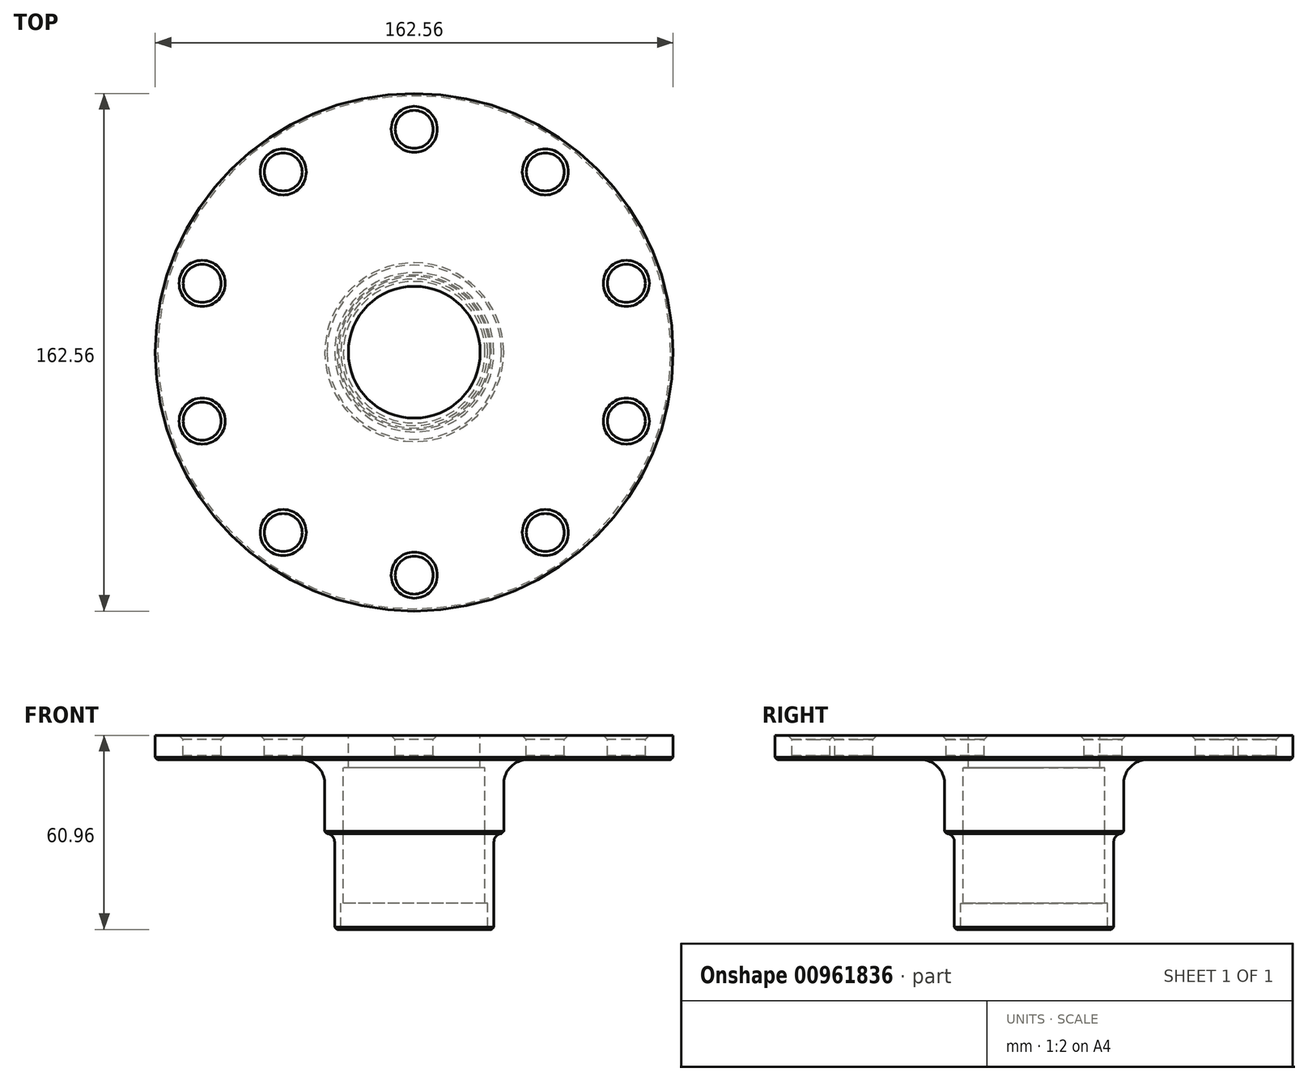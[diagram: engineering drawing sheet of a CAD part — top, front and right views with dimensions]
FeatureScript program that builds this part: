
annotation { "Feature Type Name" : "Feature", "Feature Type Description" : "" }
export const myFeature = defineFeature(function(context is Context, id is Id, definition is map)
    precondition{}
    {
        {
            var Q0;
            Q0=qCreatedBy(makeId("Top.planeOp"),FACE);
            var sketch = newSketch(context, id + "F0", { "sketchPlane" : qUnion([Q0])});
            skCircle(sketch, "E0", {"center": v(0, 0) * mm, "radius": 81.28 * mm});
            skCircle(sketch, "E1", {"center": v(0, 0) * mm, "radius": 28.08 * mm});
            skCircle(sketch, "E2", {"center": v(0, 0) * mm, "radius": 25.02 * mm});
            skCircle(sketch, "E3", {"center": v(0, 0) * mm, "radius": 69.99 * mm, "construction": true});
            skLineSegment(sketch, "E4", {"start": v(0, 0) * mm, "end": v(0, 86.5) * mm, "construction": true});
            skCircle(sketch, "E5", {"center": v(0, 69.99) * mm, "radius": 5.97 * mm});
            skCircle(sketch, "E6.1.0", {"center": v(-41.14, 56.62) * mm, "radius": 5.97 * mm});
            skCircle(sketch, "E6.2.0", {"center": v(-66.56, 21.63) * mm, "radius": 5.97 * mm});
            skCircle(sketch, "E6.3.0", {"center": v(-66.56, -21.63) * mm, "radius": 5.97 * mm});
            skCircle(sketch, "E6.4.0", {"center": v(-41.14, -56.62) * mm, "radius": 5.97 * mm});
            skCircle(sketch, "E6.5.0", {"center": v(0, -69.99) * mm, "radius": 5.97 * mm});
            skCircle(sketch, "E6.6.0", {"center": v(41.14, -56.62) * mm, "radius": 5.97 * mm});
            skCircle(sketch, "E6.7.0", {"center": v(66.56, -21.63) * mm, "radius": 5.97 * mm});
            skCircle(sketch, "E6.8.0", {"center": v(66.56, 21.63) * mm, "radius": 5.97 * mm});
            skCircle(sketch, "E6.9.0", {"center": v(41.14, 56.62) * mm, "radius": 5.97 * mm});
            skCircle(sketch, "E7", {"center": v(0, 0) * mm, "radius": 23 * mm});
            skCircle(sketch, "E8", {"center": v(0, 0) * mm, "radius": 22.23 * mm});
            skCircle(sketch, "E9", {"center": v(0, 0) * mm, "radius": 20.69 * mm});
            skSolve(sketch);
        }
        {
            var Q0;
            Q0=makeQuery(id+"F0.imprint","IMPRINT",FACE,{"disambiguationData":[TD([[makeQuery(id+"F0.imprint","IMPRINT",EDGE,{"derivedFrom":sQuery(id+"F0.wireOp",EDGE,"E0")}),1.0]])]});
            var Q1;
            Q1=makeQuery(id+"F0.imprint","IMPRINT",FACE,{"disambiguationData":[TD([[makeQuery(id+"F0.imprint","IMPRINT",EDGE,{"derivedFrom":sQuery(id+"F0.wireOp",EDGE,"E1")}),1.0]])]});
            var Q2;
            Q2=makeQuery(id+"F0.imprint","IMPRINT",FACE,{"disambiguationData":[TD([[makeQuery(id+"F0.imprint","IMPRINT",EDGE,{"derivedFrom":sQuery(id+"F0.wireOp",EDGE,"E2")}),1.0]])]});
            var Q3;
            Q3=makeQuery(id+"F0.imprint","IMPRINT",FACE,{"disambiguationData":[TD([[makeQuery(id+"F0.imprint","IMPRINT",EDGE,{"derivedFrom":sQuery(id+"F0.wireOp",EDGE,"E7")}),1.0]])]});
            var Q4;
            Q4=makeQuery(id+"F0.imprint","IMPRINT",FACE,{"disambiguationData":[TD([[makeQuery(id+"F0.imprint","IMPRINT",EDGE,{"derivedFrom":sQuery(id+"F0.wireOp",EDGE,"E8")}),1.0]])]});
            extrude(context, id + "F1", {"entities" : qUnion([Q0, Q1, Q2, Q3, Q4]), "oppositeDirection" : true, "depth" : 7.62 * mm, "offsetDistance" : 25.4 * mm});
        }
        {
            var Q0;
            Q0=makeQuery(id+"F1.opExtrude","CAP_EDGE",EDGE,{"disambiguationData":[OSD([sQuery(id+"F0.wireOp",EDGE,"E6.9.0")])],"isStart":true});
            var Q1;
            Q1=makeQuery(id+"F1.opExtrude","CAP_EDGE",EDGE,{"disambiguationData":[OSD([sQuery(id+"F0.wireOp",EDGE,"E5")])],"isStart":true});
            var Q2;
            Q2=makeQuery(id+"F1.opExtrude","CAP_EDGE",EDGE,{"disambiguationData":[OSD([sQuery(id+"F0.wireOp",EDGE,"E6.1.0")])],"isStart":true});
            var Q3;
            Q3=makeQuery(id+"F1.opExtrude","CAP_EDGE",EDGE,{"disambiguationData":[OSD([sQuery(id+"F0.wireOp",EDGE,"E6.2.0")])],"isStart":true});
            var Q4;
            Q4=makeQuery(id+"F1.opExtrude","CAP_EDGE",EDGE,{"disambiguationData":[OSD([sQuery(id+"F0.wireOp",EDGE,"E6.3.0")])],"isStart":true});
            var Q5;
            Q5=makeQuery(id+"F1.opExtrude","CAP_EDGE",EDGE,{"disambiguationData":[OSD([sQuery(id+"F0.wireOp",EDGE,"E6.4.0")])],"isStart":true});
            var Q6;
            Q6=makeQuery(id+"F1.opExtrude","CAP_EDGE",EDGE,{"disambiguationData":[OSD([sQuery(id+"F0.wireOp",EDGE,"E6.5.0")])],"isStart":true});
            var Q7;
            Q7=makeQuery(id+"F1.opExtrude","CAP_EDGE",EDGE,{"disambiguationData":[OSD([sQuery(id+"F0.wireOp",EDGE,"E6.6.0")])],"isStart":true});
            var Q8;
            Q8=makeQuery(id+"F1.opExtrude","CAP_EDGE",EDGE,{"disambiguationData":[OSD([sQuery(id+"F0.wireOp",EDGE,"E6.7.0")])],"isStart":true});
            var Q9;
            Q9=makeQuery(id+"F1.opExtrude","CAP_EDGE",EDGE,{"disambiguationData":[OSD([sQuery(id+"F0.wireOp",EDGE,"E6.8.0")])],"isStart":true});
            var Q10;
            Q10=makeQuery(id+"F1.opExtrude","CAP_EDGE",EDGE,{"disambiguationData":[OSD([sQuery(id+"F0.wireOp",EDGE,"E6.7.0")])],"isStart":false});
            var Q11;
            Q11=makeQuery(id+"F1.opExtrude","CAP_EDGE",EDGE,{"disambiguationData":[OSD([sQuery(id+"F0.wireOp",EDGE,"E6.8.0")])],"isStart":false});
            var Q12;
            Q12=makeQuery(id+"F1.opExtrude","CAP_EDGE",EDGE,{"disambiguationData":[OSD([sQuery(id+"F0.wireOp",EDGE,"E6.6.0")])],"isStart":false});
            var Q13;
            Q13=makeQuery(id+"F1.opExtrude","CAP_EDGE",EDGE,{"disambiguationData":[OSD([sQuery(id+"F0.wireOp",EDGE,"E6.5.0")])],"isStart":false});
            var Q14;
            Q14=makeQuery(id+"F1.opExtrude","CAP_EDGE",EDGE,{"disambiguationData":[OSD([sQuery(id+"F0.wireOp",EDGE,"E6.4.0")])],"isStart":false});
            var Q15;
            Q15=makeQuery(id+"F1.opExtrude","CAP_EDGE",EDGE,{"disambiguationData":[OSD([sQuery(id+"F0.wireOp",EDGE,"E6.3.0")])],"isStart":false});
            var Q16;
            Q16=makeQuery(id+"F1.opExtrude","CAP_EDGE",EDGE,{"disambiguationData":[OSD([sQuery(id+"F0.wireOp",EDGE,"E6.2.0")])],"isStart":false});
            var Q17;
            Q17=makeQuery(id+"F1.opExtrude","CAP_EDGE",EDGE,{"disambiguationData":[OSD([sQuery(id+"F0.wireOp",EDGE,"E6.1.0")])],"isStart":false});
            var Q18;
            Q18=makeQuery(id+"F1.opExtrude","CAP_EDGE",EDGE,{"disambiguationData":[OSD([sQuery(id+"F0.wireOp",EDGE,"E5")])],"isStart":false});
            var Q19;
            Q19=makeQuery(id+"F1.opExtrude","CAP_EDGE",EDGE,{"disambiguationData":[OSD([sQuery(id+"F0.wireOp",EDGE,"E6.9.0")])],"isStart":false});
            chamfer(context, id + "F2", {"entities" : qUnion([Q0, Q1, Q2, Q3, Q4, Q5, Q6, Q7, Q8, Q9, Q10, Q11, Q12, Q13, Q14, Q15, Q16, Q17, Q18, Q19]), "width" : 1.27 * mm, "tangentPropagation" : true});
        }
        {
            var Q0;
            Q0=makeQuery(id+"F0.imprint","IMPRINT",FACE,{"disambiguationData":[TD([[makeQuery(id+"F0.imprint","IMPRINT",EDGE,{"derivedFrom":sQuery(id+"F0.wireOp",EDGE,"E1")}),1.0]])]});
            var Q1;
            Q1=makeQuery(id+"F0.imprint","IMPRINT",FACE,{"disambiguationData":[TD([[makeQuery(id+"F0.imprint","IMPRINT",EDGE,{"derivedFrom":sQuery(id+"F0.wireOp",EDGE,"E2")}),1.0]])]});
            extrude(context, id + "F3", {"entities" : qUnion([Q0, Q1]), "operationType" : NewBodyOperationType.ADD, "oppositeDirection" : true, "depth" : 30.86 * mm, "offsetDistance" : 25.4 * mm});
        }
        {
            var Q0;
            Q0=makeQuery(id+"F0.imprint","IMPRINT",FACE,{"disambiguationData":[TD([[makeQuery(id+"F0.imprint","IMPRINT",EDGE,{"derivedFrom":sQuery(id+"F0.wireOp",EDGE,"E2")}),1.0]])]});
            extrude(context, id + "F4", {"entities" : qUnion([Q0]), "operationType" : NewBodyOperationType.ADD, "oppositeDirection" : true, "depth" : 60.96 * mm, "offsetDistance" : 25.4 * mm});
        }
        {
            var Q0;
            Q0=makeQuery(id+"F3.boolean.opBoolean","INTERSECT",EDGE,{"derivedFrom":[makeQuery(id+"F1.opExtrude","CAP_FACE",FACE,{"disambiguationData":[OSD([sQuery(id+"F0.wireOp",EDGE,"E0"),sQuery(id+"F0.wireOp",EDGE,"E5"),sQuery(id+"F0.wireOp",EDGE,"E6.1.0"),sQuery(id+"F0.wireOp",EDGE,"E6.2.0"),sQuery(id+"F0.wireOp",EDGE,"E6.3.0"),sQuery(id+"F0.wireOp",EDGE,"E6.4.0"),sQuery(id+"F0.wireOp",EDGE,"E6.5.0"),sQuery(id+"F0.wireOp",EDGE,"E6.6.0"),sQuery(id+"F0.wireOp",EDGE,"E6.7.0"),sQuery(id+"F0.wireOp",EDGE,"E6.8.0"),sQuery(id+"F0.wireOp",EDGE,"E6.9.0"),sQuery(id+"F0.wireOp",EDGE,"E9")])],"isStart":false}),makeQuery(id+"F3.opExtrude","SWEPT_FACE",FACE,{"disambiguationData":[OSD([sQuery(id+"F0.wireOp",EDGE,"E1")])]})]});
            fillet(context, id + "F5", {"entities" : qUnion([Q0]), "radius" : 7.62 * mm, "tangentPropagation" : true, "allowEdgeOverflow" : false});
        }
        {
            var Q0;
            Q0=makeQuery(id+"F4.boolean.opBoolean","INTERSECT",EDGE,{"derivedFrom":[makeQuery(id+"F3.opExtrude","CAP_FACE",FACE,{"disambiguationData":[OSD([sQuery(id+"F0.wireOp",EDGE,"E1"),sQuery(id+"F0.wireOp",EDGE,"E7")])],"isStart":false}),makeQuery(id+"F4.opExtrude","SWEPT_FACE",FACE,{"disambiguationData":[OSD([sQuery(id+"F0.wireOp",EDGE,"E2")])]})]});
            fillet(context, id + "F6", {"entities" : qUnion([Q0]), "radius" : 2.54 * mm, "tangentPropagation" : true, "allowEdgeOverflow" : false});
        }
        {
            var Q0;
            Q0=makeQuery(id+"F1.opExtrude","CAP_EDGE",EDGE,{"disambiguationData":[OSD([sQuery(id+"F0.wireOp",EDGE,"E0")])],"isStart":false});
            var Q1;
            Q1=makeQuery(id+"F3.opExtrude","CAP_EDGE",EDGE,{"disambiguationData":[OSD([sQuery(id+"F0.wireOp",EDGE,"E1")])],"isStart":false});
            var Q2;
            Q2=makeQuery(id+"F4.opExtrude","CAP_EDGE",EDGE,{"disambiguationData":[OSD([sQuery(id+"F0.wireOp",EDGE,"E2")])],"isStart":false});
            var Q3;
            Q3=makeQuery(id+"F4.opExtrude","CAP_EDGE",EDGE,{"disambiguationData":[OSD([sQuery(id+"F0.wireOp",EDGE,"E7")])],"isStart":false});
            chamfer(context, id + "F7", {"entities" : qUnion([Q0, Q1, Q2, Q3]), "width" : 0.76 * mm, "tangentPropagation" : true});
        }
        {
            var Q0;
            Q0=makeQuery(id+"F0.imprint","IMPRINT",FACE,{"disambiguationData":[TD([[makeQuery(id+"F0.imprint","IMPRINT",EDGE,{"derivedFrom":sQuery(id+"F0.wireOp",EDGE,"E8")}),1.0]])]});
            extrude(context, id + "F8", {"entities" : qUnion([Q0]), "operationType" : NewBodyOperationType.ADD, "oppositeDirection" : true, "depth" : 10.16 * mm, "offsetDistance" : 25.4 * mm});
        }
        {
            var Q0;
            {var subQ0=sQuery(id+"F0.wireOp",EDGE,"E9");Q0=makeQuery(id+"F3.boolean.opBoolean","SPLIT",FACE,{"disambiguationData":[TD([makeQuery(id+"F1.opExtrude","SWEPT_FACE",FACE,{"disambiguationData":[OSD([subQ0])]})])],"derivedFrom":makeQuery(id+"F1.opExtrude","CAP_FACE",FACE,{"disambiguationData":[OSD([sQuery(id+"F0.wireOp",EDGE,"E0"),sQuery(id+"F0.wireOp",EDGE,"E5"),sQuery(id+"F0.wireOp",EDGE,"E6.1.0"),sQuery(id+"F0.wireOp",EDGE,"E6.2.0"),sQuery(id+"F0.wireOp",EDGE,"E6.3.0"),sQuery(id+"F0.wireOp",EDGE,"E6.4.0"),sQuery(id+"F0.wireOp",EDGE,"E6.5.0"),sQuery(id+"F0.wireOp",EDGE,"E6.6.0"),sQuery(id+"F0.wireOp",EDGE,"E6.7.0"),sQuery(id+"F0.wireOp",EDGE,"E6.8.0"),sQuery(id+"F0.wireOp",EDGE,"E6.9.0"),subQ0])],"isStart":false})});}
            extrude(context, id + "F9", {"entities" : qUnion([Q0]), "operationType" : NewBodyOperationType.ADD, "depth" : 45.08 * mm, "offsetDistance" : 25.4 * mm});
        }
    });
